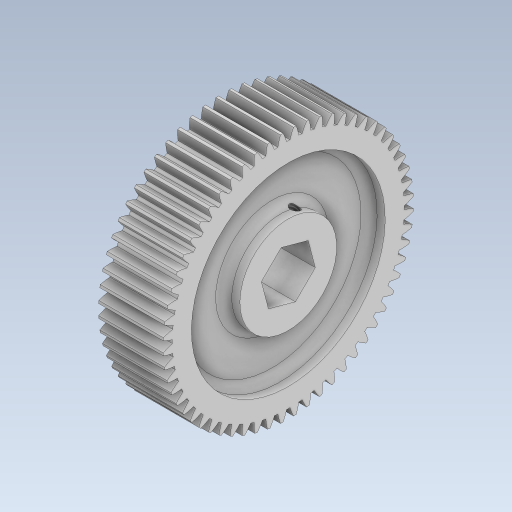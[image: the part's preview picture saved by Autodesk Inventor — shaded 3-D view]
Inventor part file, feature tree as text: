
AUTODESK INVENTOR PART (.ipt)
format: ipt  version: 2023 (Build 270158000, 158)  size: 588,800 bytes
history: native  units: in
note: dims shown in document units (in); Inventor stores cm internally (conversion verified against a paired STEP export)
features: sketch x5, extrude x3, plane x3, fillet x1, hole x1, mirror x1, other x1
ambient origin geometry x8: Origin, YZ Plane, XZ Plane, XY Plane, X Axis, Y Axis, Z Axis, Center Point
bodies: Solid1 (feature_tree)
feature tree (15):
  extrude  "Extrusion1"  TaperAngle=0.0deg  [1 undecoded]
  extrude  "Extrusion2"  Depth=0.375in
  extrude  "Extrusion3"  Depth=0.125in
  fillet  "Fillet1"  Radius=0.125in
  plane  "Work Plane1"
  plane  "Work Plane2"
  sketch  "Sketch4"  dims[d11=0.0625in d12=-0.25in]
  plane  "Work Plane3"
  hole  "Hole1"  [1 undecoded]
  mirror  "Mirror2"
  sketch  "Sketch1"  dims[d0=0.5in d1=0.0in d2=0.0in]
  sketch  "Sketch2"  dims[d4=0.0in d5=0.0in d6=0.375in]
  sketch  "Sketch3"  dims[d7=0.75in d8=1.5in d9=0.125in d10=0.0in]
  sketch  "Sketch5"  dims[d13=-0.1875in d14=15.0deg d15=0.0625in d16=0.0764in d17=0.198in d18=0.435in d19=0.15in d20=0.563in d21=1.0in d22=0.8108in]
  other  "TeethCuts"
note: 2 required parameter values undecoded (feature->parameter linkage not recoverable at this tier; creation-order binding heuristic only, values carry confidence <= 0.55)
